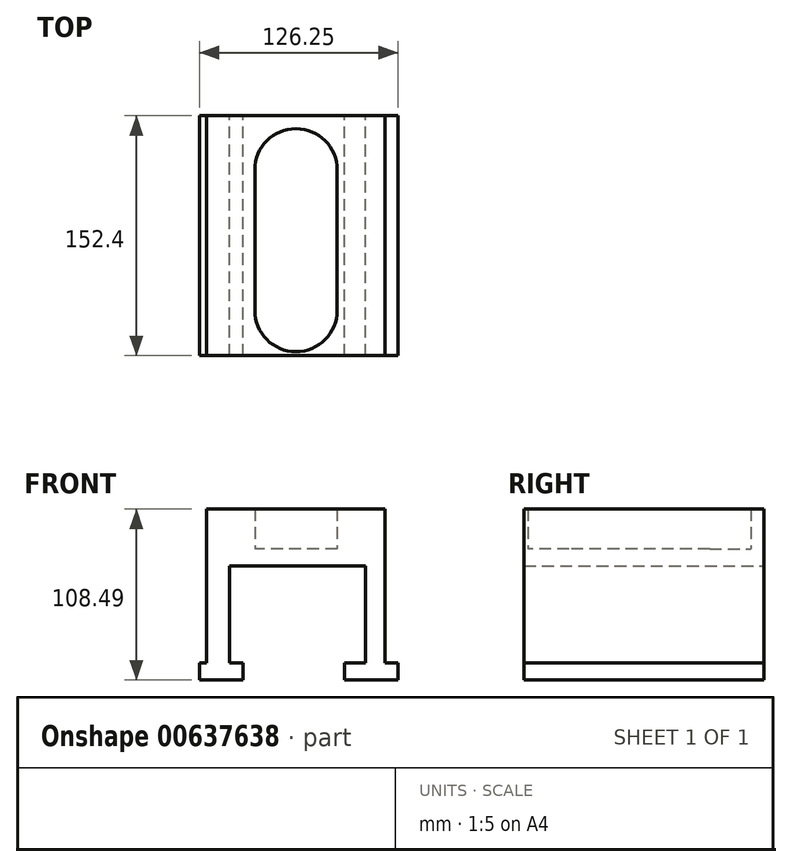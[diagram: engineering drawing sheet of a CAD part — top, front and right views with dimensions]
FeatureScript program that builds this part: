
annotation { "Feature Type Name" : "Feature", "Feature Type Description" : "" }
export const myFeature = defineFeature(function(context is Context, id is Id, definition is map)
    precondition{}
    {
        {
            var Q0;
            Q0=qCreatedBy(makeId("Front.planeOp"),FACE);
            var sketch = newSketch(context, id + "F0", { "sketchPlane" : qUnion([Q0])});
            skLineSegment(sketch, "E0", {"start": v(-66.5, -21.73) * mm, "end": v(-66.5, -32.6) * mm});
            skLineSegment(sketch, "E1", {"start": v(-66.5, -32.6) * mm, "end": v(-38.61, -32.6) * mm});
            skLineSegment(sketch, "E2", {"start": v(-38.61, -32.6) * mm, "end": v(-38.61, -21.73) * mm});
            skLineSegment(sketch, "E3", {"start": v(-38.61, -21.73) * mm, "end": v(-47.42, -21.73) * mm});
            skLineSegment(sketch, "E4", {"start": v(-47.42, -21.73) * mm, "end": v(-47.42, 39.93) * mm});
            skLineSegment(sketch, "E5", {"start": v(-47.42, 39.93) * mm, "end": v(38.9, 39.93) * mm});
            skLineSegment(sketch, "E6", {"start": v(38.9, 39.93) * mm, "end": v(38.9, -21.73) * mm});
            skLineSegment(sketch, "E7", {"start": v(38.9, -21.73) * mm, "end": v(25.7, -21.73) * mm});
            skLineSegment(sketch, "E8", {"start": v(25.7, -21.73) * mm, "end": v(25.7, -32.6) * mm});
            skLineSegment(sketch, "E9", {"start": v(25.7, -32.6) * mm, "end": v(59.75, -32.6) * mm});
            skLineSegment(sketch, "E10", {"start": v(59.75, -32.6) * mm, "end": v(59.75, -21.73) * mm});
            skLineSegment(sketch, "E11", {"start": v(59.75, -21.73) * mm, "end": v(51.53, -21.73) * mm});
            skLineSegment(sketch, "E12", {"start": v(51.53, -21.73) * mm, "end": v(51.53, 50.5) * mm});
            skLineSegment(sketch, "E13", {"start": v(51.53, 50.5) * mm, "end": v(-61.8, 50.5) * mm});
            skLineSegment(sketch, "E14", {"start": v(-61.8, 50.5) * mm, "end": v(-61.8, -21.73) * mm});
            skLineSegment(sketch, "E15", {"start": v(-61.8, -21.73) * mm, "end": v(-66.5, -21.73) * mm});
            skSolve(sketch);
        }
        {
            var Q0;
            Q0 = qSketchRegion(id + "F0", true);
            var Q1;
            Q1 = qSketchRegion(id + "Fy4T8KILkSUWa7b_1", true);
            extrude(context, id + "F1", {"entities" : qUnion([Q0, Q1]), "depth" : 152.4 * mm, "offsetDistance" : 25.4 * mm});
        }
        {
            var Q0;
            Q0=makeQuery(id+"F1.opExtrude","SWEPT_FACE",FACE,{"disambiguationData":[OSD([sQuery(id+"F0.wireOp",EDGE,"E13")])]});
            var sketch = newSketch(context, id + "F2", { "sketchPlane" : qUnion([Q0])});
            skLineSegment(sketch, "E16", {"start": v(-31.3, -34.43) * mm, "end": v(-31.3, -123.8) * mm});
            skLineSegment(sketch, "E17", {"start": v(21.02, -34.43) * mm, "end": v(21.02, -123.8) * mm});
            skArc(sketch, "E18", {"start": v(21.02, -34.43) * mm, "mid": v(-5.14, -8.27) * mm, "end": v(-31.3, -34.43) * mm});
            skArc(sketch, "E19", {"start": v(-31.3, -123.8) * mm, "mid": v(-5.14, -149.95) * mm, "end": v(21.02, -123.8) * mm});
            skPoint(sketch, "E20.start.orphan", {"position": v(-31.3, -79.11) * mm});
            skPoint(sketch, "E21.start.orphan", {"position": v(21.02, -79.11) * mm});
            skSolve(sketch);
        }
        {
            var Q0;
            Q0=makeQuery(id+"F2.imprint","IMPRINT",FACE,{"disambiguationData":[TD([[makeQuery(id+"F2.imprint","IMPRINT",EDGE,{"derivedFrom":sQuery(id+"F2.wireOp",EDGE,"E16")}),-1.0]])]});
            extrude(context, id + "F3", {"entities" : qUnion([Q0]), "operationType" : NewBodyOperationType.ADD, "depth" : 25.4 * mm, "offsetDistance" : 25.4 * mm});
        }
    });
